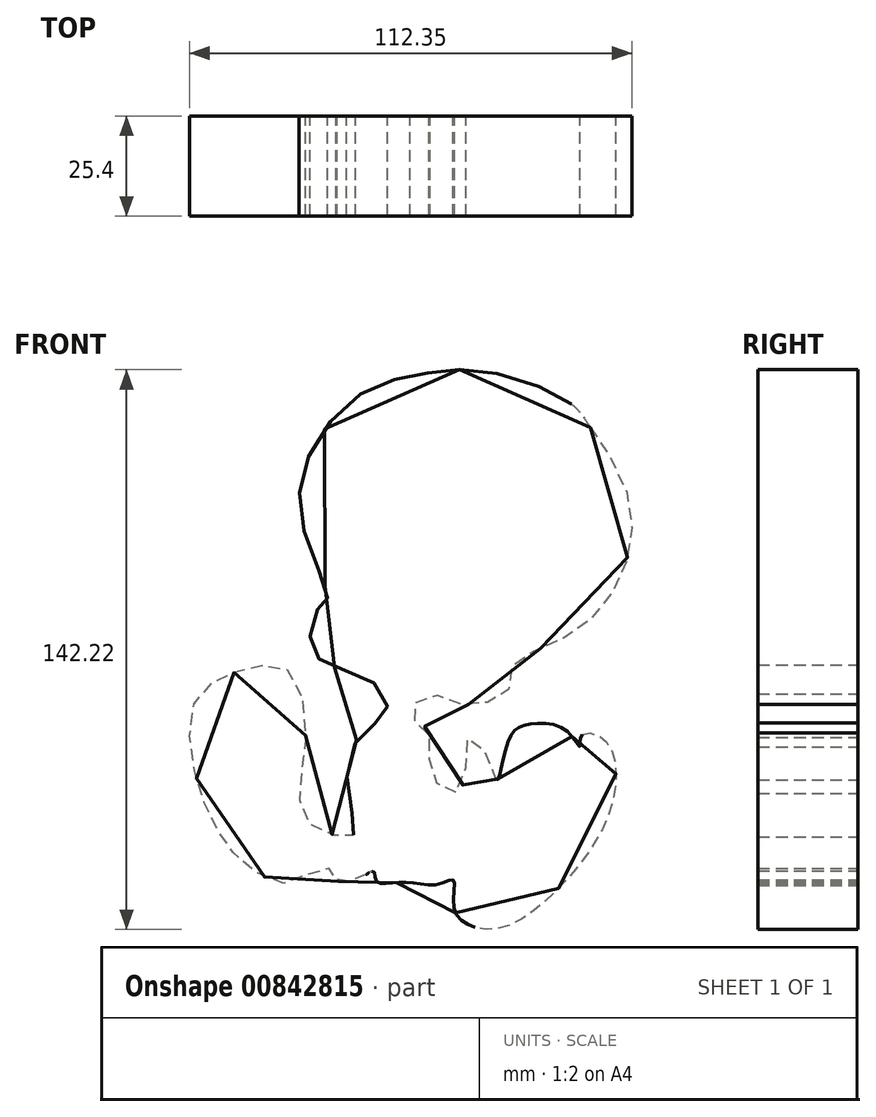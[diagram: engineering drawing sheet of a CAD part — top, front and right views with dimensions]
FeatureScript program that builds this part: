
annotation { "Feature Type Name" : "Feature", "Feature Type Description" : "" }
export const myFeature = defineFeature(function(context is Context, id is Id, definition is map)
    precondition{}
    {
        {
            var Q0;
            Q0=qCreatedBy(makeId("Front.planeOp"),FACE);
            var sketch = newSketch(context, id + "F0", { "sketchPlane" : qUnion([Q0])});
            skPoint(sketch, "E0.79.internal.snap0", {"position": v(-62.95, 5.34) * mm});
            skFitSpline(sketch, "E0", {"points": [v(-11.37, 58.67) * mm, v(-17.27, 54.62) * mm, v(-23.5, 47.54) * mm, v(-27.04, 39.12) * mm, v(-27.2, 31.03) * mm, v(-25.86, 22.27) * mm, v(-23.33, 13.84) * mm, v(-20.8, 7.27) * mm, v(-24, 2.55) * mm, v(-25.35, -1.66) * mm, v(-21.64, -9.15) * mm, v(-11.77, -12.6) * mm, v(-8.14, -15.46) * mm, v(-6.78, -21.94) * mm, v(-11.62, -25.35) * mm, v(-14.8, -35.97) * mm, v(-15.05, -43.4) * mm, v(-14.02, -52.2) * mm, v(-17.2, -53.23) * mm, v(-21.8, -52.38) * mm, v(-26.47, -48.55) * mm, v(-27.6, -42.55) * mm, v(-27.12, -33.47) * mm, v(-26.34, -25.24) * mm, v(-26.96, -18.93) * mm, v(-31.65, -10.8) * mm, v(-42.06, -10.53) * mm, v(-48.92, -12.73) * mm, v(-52, -15.58) * mm, v(-54.81, -20.59) * mm, v(-55.9, -28.15) * mm, v(-54.7, -37.13) * mm, v(-51.52, -45.7) * mm, v(-47.75, -51.64) * mm, v(-42.53, -58.63) * mm, v(-36.73, -63.17) * mm, v(-30.5, -64.75) * mm, v(-22.13, -62.12) * mm, v(-19.32, -62.07) * mm, v(-18.91, -64.74) * mm, v(-14.1, -64.6) * mm, v(-9.89, -62.13) * mm, v(-8.12, -63.53) * mm, v(-6.71, -66.07) * mm, v(-3.86, -65.03) * mm, v(0, -64.16) * mm, v(3.23, -65.65) * mm, v(7.21, -65.32) * mm, v(9.6, -63.43) * mm, v(11.42, -63.18) * mm, v(10.93, -67.79) * mm, v(11.9, -73.29) * mm, v(16.13, -75.61) * mm, v(21.07, -76.31) * mm, v(24.76, -74.81) * mm, v(33.31, -70.6) * mm, v(40.73, -62.87) * mm, v(46.2, -56.42) * mm, v(51.04, -47.4) * mm, v(52.33, -35.79) * mm, v(47.5, -27.08) * mm, v(42.34, -26.76) * mm, v(35.9, -24.5) * mm, v(25.9, -27.08) * mm, v(23.32, -33.53) * mm, v(21.7, -39.01) * mm, v(18.8, -31.6) * mm, v(14.94, -27.4) * mm, v(14.3, -35.46) * mm, v(13, -40.95) * mm, v(13, -42.88) * mm, v(7.84, -38.69) * mm, v(5.59, -30.3) * mm, v(0, -23.21) * mm, v(4.62, -17.73) * mm, v(16.23, -19.99) * mm, v(24.6, -15.48) * mm, v(25.9, -9.35) * mm, v(38.15, -3.55) * mm, v(48.14, 5.34) * mm, v(54.91, 15.47) * mm, v(55.56, 29.98) * mm, v(51.04, 45.13) * mm, v(41.05, 55.77) * mm, v(28.48, 62.22) * mm, v(18.48, 63.83) * mm, v(5.9, 65.12) * mm, v(-4.4, 62.54) * mm, v(-11.37, 58.67) * mm]});
            skSolve(sketch);
        }
        {
            var Q0;
            Q0=makeQuery(id+"F0.imprint","IMPRINT",FACE,{"disambiguationData":[TD([[makeQuery(id+"F0.imprint","IMPRINT",EDGE,{"derivedFrom":sQuery(id+"F0.wireOp",EDGE,"E0")}),1.0]])]});
            var sketch = newSketch(context, id + "F1", { "sketchPlane" : qUnion([Q0])});
            skFitSpline(sketch, "E1", {"points": [v(45.77, 50.57) * mm, v(54.08, 36.83) * mm, v(56.19, 22.52) * mm, v(52.2, 10.08) * mm, v(43.75, 0) * mm, v(32.5, -5.88) * mm, v(25.69, -10.57) * mm, v(24.75, -16.67) * mm, v(17.24, -19.72) * mm, v(9.96, -19.02) * mm, v(3.86, -17.37) * mm, v(0, -23) * mm, v(3.4, -25.12) * mm, v(5.04, -30.51) * mm, v(5.28, -37.08) * mm, v(10.25, -42.41) * mm, v(13.94, -38.72) * mm, v(14.73, -28.45) * mm, v(18.68, -31.09) * mm, v(22.1, -38.99) * mm, v(25, -28.98) * mm, v(29.48, -25.03) * mm, v(39.48, -26.34) * mm, v(43.17, -30.56) * mm, v(43.43, -27.93) * mm, v(47.65, -27.66) * mm, v(51.86, -33.46) * mm, v(50.8, -46.89) * mm, v(44.49, -58.48) * mm, v(36.85, -67.43) * mm, v(24.73, -76.12) * mm, v(15.52, -76.12) * mm, v(11.04, -71.12) * mm, v(11.04, -64.53) * mm, v(7.09, -65.59) * mm, v(0, -65.06) * mm, v(-5.82, -65.32) * mm, v(-8.72, -64.53) * mm, v(-9.24, -62.16) * mm, v(-13.46, -64.53) * mm, v(-16.62, -64.8) * mm, v(-18.72, -64.53) * mm, v(-18.72, -62.16) * mm, v(-25.83, -62.7) * mm, v(-31.1, -65.32) * mm, v(-41.11, -61.1) * mm, v(-47.7, -53.73) * mm, v(-52.7, -43.6) * mm, v(-55.9, -29.37) * mm, v(-53.52, -17.13) * mm, v(-44.86, -11.75) * mm, v(-37.7, -9.96) * mm, v(-29.93, -12.05) * mm, v(-26.65, -30.56) * mm, v(-28.14, -41.6) * mm, v(-26.05, -49.67) * mm, v(-17.99, -53.25) * mm, v(-14.1, -52.65) * mm, v(-15.9, -41.9) * mm, v(-12.32, -27.28) * mm, v(-6.05, -21.9) * mm, v(-9.33, -14.14) * mm, v(-21.54, -9.38) * mm, v(-25.4, -2.85) * mm, v(-22.43, 5.76) * mm, v(-20.95, 7.24) * mm, v(-26.59, 22.97) * mm, v(-26.3, 41.97) * mm, v(-12.34, 59.19) * mm, v(3.69, 64.23) * mm, v(18.83, 64.83) * mm, v(40.2, 57.1) * mm, v(45.77, 50.57) * mm]});
            skSolve(sketch);
        }
        {
            var Q0;
            Q0 = qSketchRegion(id + "F1", true);
            extrude(context, id + "F2", {"entities" : qUnion([Q0]), "depth" : 25.4 * mm, "offsetDistance" : 25.4 * mm});
        }
    });
